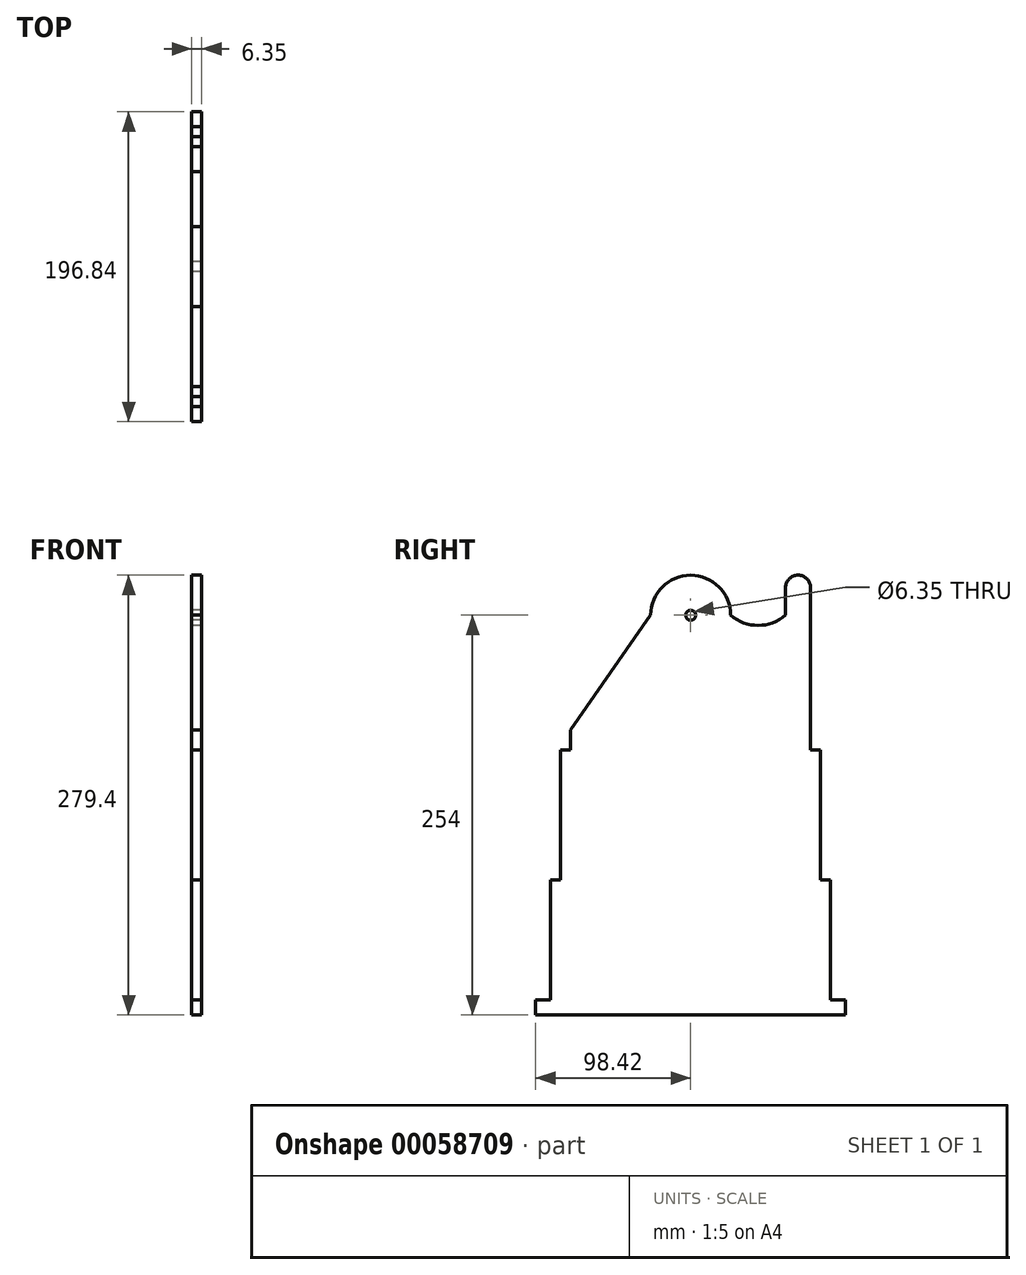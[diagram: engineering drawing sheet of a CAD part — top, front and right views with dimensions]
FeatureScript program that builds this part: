
annotation { "Feature Type Name" : "Feature", "Feature Type Description" : "" }
export const myFeature = defineFeature(function(context is Context, id is Id, definition is map)
    precondition{}
    {
        {
            var Q0;
            Q0=qCreatedBy(makeId("Right.planeOp"),FACE);
            var sketch = newSketch(context, id + "F0", { "sketchPlane" : qUnion([Q0])});
            skLineSegment(sketch, "E0", {"start": v(-88.9, -130.18) * mm, "end": v(-88.9, -53.97) * mm});
            skLineSegment(sketch, "E1", {"start": v(-88.9, -53.98) * mm, "end": v(-82.55, -53.98) * mm});
            skLineSegment(sketch, "E2", {"start": v(82.55, -53.98) * mm, "end": v(88.9, -53.98) * mm});
            skLineSegment(sketch, "E3", {"start": v(-82.55, 28.58) * mm, "end": v(-76.2, 28.58) * mm});
            skLineSegment(sketch, "E4", {"start": v(76.2, 28.58) * mm, "end": v(82.55, 28.58) * mm});
            skLineSegment(sketch, "E5", {"start": v(88.9, -53.98) * mm, "end": v(88.9, -130.18) * mm});
            skLineSegment(sketch, "E6", {"start": v(-82.55, -53.98) * mm, "end": v(-82.55, 28.58) * mm});
            skLineSegment(sketch, "E7", {"start": v(82.55, -53.98) * mm, "end": v(82.55, 28.58) * mm});
            skArc(sketch, "E8", {"start": v(25.4, 114.3) * mm, "mid": v(0, 139.7) * mm, "end": v(-25.4, 114.3) * mm});
            skLineSegment(sketch, "E9", {"start": v(-25.4, 114.3) * mm, "end": v(-76.2, 41.28) * mm});
            skCircle(sketch, "E10", {"center": v(0, 114.3) * mm, "radius": 3.18 * mm});
            skLineSegment(sketch, "E11", {"start": v(-76.2, 28.58) * mm, "end": v(-76.2, 41.28) * mm});
            skLineSegment(sketch, "E12", {"start": v(76.2, 28.58) * mm, "end": v(76.2, 34.93) * mm});
            skLineSegment(sketch, "E13", {"start": v(-88.9, -130.18) * mm, "end": v(-98.43, -130.18) * mm});
            skLineSegment(sketch, "E14", {"start": v(-98.43, -130.18) * mm, "end": v(-98.43, -139.7) * mm});
            skLineSegment(sketch, "E15", {"start": v(-98.43, -139.7) * mm, "end": v(98.43, -139.7) * mm});
            skLineSegment(sketch, "E16", {"start": v(88.9, -130.18) * mm, "end": v(98.43, -130.18) * mm});
            skLineSegment(sketch, "E17", {"start": v(98.43, -130.18) * mm, "end": v(98.43, -139.7) * mm});
            skLineSegment(sketch, "E18", {"start": v(76.2, 131.76) * mm, "end": v(76.2, 34.93) * mm});
            skArc(sketch, "E19", {"start": v(25.4, 114.3) * mm, "mid": v(42.86, 107.81) * mm, "end": v(60.33, 114.3) * mm});
            skLineSegment(sketch, "E20", {"start": v(60.33, 114.3) * mm, "end": v(60.33, 131.76) * mm});
            skArc(sketch, "E21", {"start": v(76.2, 131.76) * mm, "mid": v(68.26, 139.7) * mm, "end": v(60.33, 131.76) * mm});
            skSolve(sketch);
        }
        {
            var Q0;
            Q0 = qSketchRegion(id + "F0", true);
            extrude(context, id + "F1", {"entities" : qUnion([Q0]), "depth" : 6.35 * mm});
        }
    });
